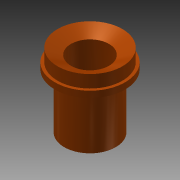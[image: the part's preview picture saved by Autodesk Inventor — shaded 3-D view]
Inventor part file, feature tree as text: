
AUTODESK INVENTOR PART (.ipt)
format: ipt  version: 2015 (Build 190159000, 159)  size: 144,384 bytes
history: native  units: in
note: dims shown in document units (in); Inventor stores cm internally (conversion verified against a paired STEP export)
features: revolve x1, sketch x1
ambient origin geometry x8: Origin, YZ Plane, XZ Plane, XY Plane, X Axis, Y Axis, Z Axis, Center Point
bodies: Solid1 (feature_tree)
feature tree (2):
  revolve  "Revolution1"  [1 undecoded]
  sketch  "Sketch1"  dims[d25=90.0deg d86=0.75in d87=1.0in d88=0.2185in d89=2.594in d90=0.5in d91=0.5in d92=1.75in d93=0.25in d94=105.0deg d95=0.5in d96=0.5in d97=0.25in d98=0.375in d99=2.0in d100=0.5in d101=0.25in d102=0.234in d103=0.25in d104=2.0in d105=0.25in d106=105.0deg d107=0.125in d108=0.25in d109=2.3995in d110=0.125in d111=0.25in d112=1.0in d113=0.1718in d114=1.6531in d115=1.2713in d116=90.0deg d117=3.1729in]
note: 1 required parameter value undecoded (feature->parameter linkage not recoverable at this tier; creation-order binding heuristic only, values carry confidence <= 0.55)
